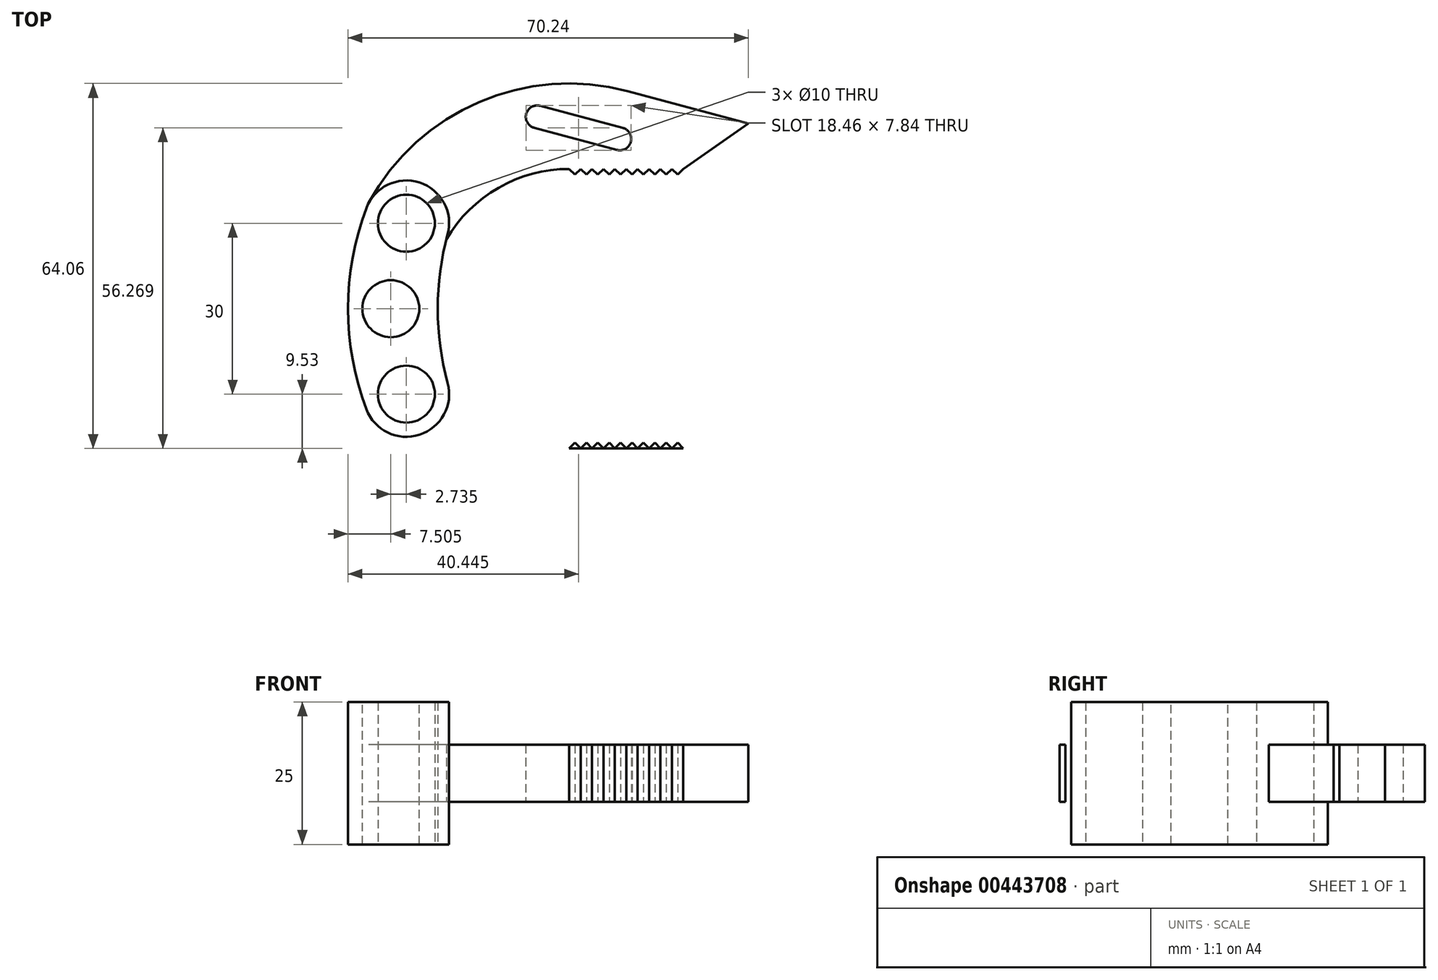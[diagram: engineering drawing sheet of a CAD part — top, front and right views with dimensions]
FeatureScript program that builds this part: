
annotation { "Feature Type Name" : "Feature", "Feature Type Description" : "" }
export const myFeature = defineFeature(function(context is Context, id is Id, definition is map)
    precondition{}
    {
        {
            var Q0;
            Q0=qCreatedBy(makeId("Top.planeOp"),FACE);
            var sketch = newSketch(context, id + "F0", { "sketchPlane" : qUnion([Q0])});
            skLineSegment(sketch, "E0", {"start": v(0, 15) * mm, "end": v(0, -15) * mm, "construction": true});
            skArc(sketch, "E1", {"start": v(7.24, 13.04) * mm, "mid": v(2.3, 22.14) * mm, "end": v(-7.02, 17.65) * mm});
            skArc(sketch, "E2", {"start": v(-7.02, -17.65) * mm, "mid": v(2.3, -22.14) * mm, "end": v(7.24, -13.04) * mm});
            skArc(sketch, "E3", {"start": v(-7.02, 17.65) * mm, "mid": v(-10.24, 0) * mm, "end": v(-7.02, -17.65) * mm});
            skArc(sketch, "E4", {"start": v(7.24, 13.04) * mm, "mid": v(5.5, 0) * mm, "end": v(7.24, -13.04) * mm});
            skCircle(sketch, "E5", {"center": v(0, 15) * mm, "radius": 5 * mm});
            skCircle(sketch, "E6", {"center": v(0, -15) * mm, "radius": 5 * mm});
            skSolve(sketch);
        }
        {
            var Q0;
            Q0=qCreatedBy(makeId("Top.planeOp"),FACE);
            var sketch = newSketch(context, id + "F1", { "sketchPlane" : qUnion([Q0])});
            skCircle(sketch, "E7.0", {"center": v(0, 15) * mm, "radius": 5 * mm});
            skArc(sketch, "E8", {"start": v(-6.6, 18.57) * mm, "mid": v(-3.57, 8.4) * mm, "end": v(6.6, 11.43) * mm});
            skArc(sketch, "E9", {"start": v(38.92, 38.17) * mm, "mid": v(12.76, 36.27) * mm, "end": v(-6.6, 18.57) * mm});
            skArc(sketch, "E10", {"start": v(28.58, 24.53) * mm, "mid": v(15.79, 21) * mm, "end": v(6.6, 11.43) * mm});
            skLineSegment(sketch, "E11", {"start": v(28.58, 24.53) * mm, "end": v(48.58, 24.53) * mm});
            skLineSegment(sketch, "E12", {"start": v(48.58, 24.53) * mm, "end": v(60, 32.53) * mm});
            skLineSegment(sketch, "E13", {"start": v(60, 32.53) * mm, "end": v(38.92, 38.17) * mm});
            skLineSegment(sketch, "E14", {"start": v(38.92, 38.17) * mm, "end": v(37.45, 29.8) * mm, "construction": true});
            skLineSegment(sketch, "E15", {"start": v(37.45, 29.8) * mm, "end": v(22.96, 33.68) * mm, "construction": true});
            skCircle(sketch, "E16", {"center": v(22.96, 33.68) * mm, "radius": 2 * mm});
            skCircle(sketch, "E17", {"center": v(37.45, 29.8) * mm, "radius": 2 * mm});
            skLineSegment(sketch, "E18", {"start": v(23.48, 35.6) * mm, "end": v(37.97, 31.73) * mm});
            skLineSegment(sketch, "E19", {"start": v(22.44, 31.75) * mm, "end": v(36.93, 27.87) * mm});
            skLineSegment(sketch, "E20", {"start": v(0, 0) * mm, "end": v(59.7, 0) * mm, "construction": true});
            skLineSegment(sketch, "E21", {"start": v(28.58, 24.53) * mm, "end": v(29.58, 23.53) * mm});
            skLineSegment(sketch, "E22", {"start": v(29.58, 23.53) * mm, "end": v(30.58, 24.53) * mm});
            skLineSegment(sketch, "E23.1.0.0", {"start": v(30.58, 24.53) * mm, "end": v(31.58, 23.53) * mm});
            skLineSegment(sketch, "E23.1.0.1", {"start": v(31.58, 23.53) * mm, "end": v(32.58, 24.53) * mm});
            skLineSegment(sketch, "E23.2.0.0", {"start": v(32.58, 24.53) * mm, "end": v(33.58, 23.53) * mm});
            skLineSegment(sketch, "E23.2.0.1", {"start": v(33.58, 23.53) * mm, "end": v(34.58, 24.53) * mm});
            skLineSegment(sketch, "E23.3.0.0", {"start": v(34.58, 24.53) * mm, "end": v(35.58, 23.53) * mm});
            skLineSegment(sketch, "E23.3.0.1", {"start": v(35.58, 23.53) * mm, "end": v(36.58, 24.53) * mm});
            skLineSegment(sketch, "E23.4.0.0", {"start": v(36.58, 24.53) * mm, "end": v(37.58, 23.53) * mm});
            skLineSegment(sketch, "E23.4.0.1", {"start": v(37.58, 23.53) * mm, "end": v(38.58, 24.53) * mm});
            skLineSegment(sketch, "E23.5.0.0", {"start": v(38.58, 24.53) * mm, "end": v(39.58, 23.53) * mm});
            skLineSegment(sketch, "E23.5.0.1", {"start": v(39.58, 23.53) * mm, "end": v(40.58, 24.53) * mm});
            skLineSegment(sketch, "E23.6.0.0", {"start": v(40.58, 24.53) * mm, "end": v(41.58, 23.53) * mm});
            skLineSegment(sketch, "E23.6.0.1", {"start": v(41.58, 23.53) * mm, "end": v(42.58, 24.53) * mm});
            skLineSegment(sketch, "E23.7.0.0", {"start": v(42.58, 24.53) * mm, "end": v(43.58, 23.53) * mm});
            skLineSegment(sketch, "E23.7.0.1", {"start": v(43.58, 23.53) * mm, "end": v(44.58, 24.53) * mm});
            skLineSegment(sketch, "E23.8.0.0", {"start": v(44.58, 24.53) * mm, "end": v(45.58, 23.53) * mm});
            skLineSegment(sketch, "E23.8.0.1", {"start": v(45.58, 23.53) * mm, "end": v(46.58, 24.53) * mm});
            skLineSegment(sketch, "E23.9.0.0", {"start": v(46.58, 24.53) * mm, "end": v(47.58, 23.53) * mm});
            skLineSegment(sketch, "E23.9.0.1", {"start": v(47.58, 23.53) * mm, "end": v(48.58, 24.53) * mm});
            skLineSegment(sketch, "E23.direction1", {"start": v(29.58, 23.53) * mm, "end": v(31.58, 23.53) * mm, "construction": true});
            skLineSegment(sketch, "E24.MirrorCS", {"start": v(29.58, -23.53) * mm, "end": v(30.58, -24.53) * mm});
            skLineSegment(sketch, "E25.MirrorCS", {"start": v(39.58, -23.53) * mm, "end": v(40.58, -24.53) * mm});
            skLineSegment(sketch, "E26.MirrorCS", {"start": v(30.58, -24.53) * mm, "end": v(31.58, -23.53) * mm});
            skLineSegment(sketch, "E27.MirrorCS", {"start": v(29.58, -23.53) * mm, "end": v(31.58, -23.53) * mm, "construction": true});
            skLineSegment(sketch, "E28.MirrorCS", {"start": v(32.58, -24.53) * mm, "end": v(33.58, -23.53) * mm});
            skLineSegment(sketch, "E29.MirrorCS", {"start": v(33.58, -23.53) * mm, "end": v(34.58, -24.53) * mm});
            skLineSegment(sketch, "E30.MirrorCS", {"start": v(41.58, -23.53) * mm, "end": v(42.58, -24.53) * mm});
            skLineSegment(sketch, "E31.MirrorCS", {"start": v(31.58, -23.53) * mm, "end": v(32.58, -24.53) * mm});
            skLineSegment(sketch, "E32.MirrorCS", {"start": v(40.58, -24.53) * mm, "end": v(41.58, -23.53) * mm});
            skLineSegment(sketch, "E33.MirrorCS", {"start": v(28.58, -24.53) * mm, "end": v(29.58, -23.53) * mm});
            skLineSegment(sketch, "E34.MirrorCS", {"start": v(45.58, -23.53) * mm, "end": v(46.58, -24.53) * mm});
            skLineSegment(sketch, "E35.MirrorCS", {"start": v(42.58, -24.53) * mm, "end": v(43.58, -23.53) * mm});
            skLineSegment(sketch, "E36.MirrorCS", {"start": v(36.58, -24.53) * mm, "end": v(37.58, -23.53) * mm});
            skLineSegment(sketch, "E37.MirrorCS", {"start": v(37.58, -23.53) * mm, "end": v(38.58, -24.53) * mm});
            skLineSegment(sketch, "E38.MirrorCS", {"start": v(38.58, -24.53) * mm, "end": v(39.58, -23.53) * mm});
            skLineSegment(sketch, "E39.MirrorCS", {"start": v(44.58, -24.53) * mm, "end": v(45.58, -23.53) * mm});
            skLineSegment(sketch, "E40.MirrorCS", {"start": v(35.58, -23.53) * mm, "end": v(36.58, -24.53) * mm});
            skLineSegment(sketch, "E41.MirrorCS", {"start": v(43.58, -23.53) * mm, "end": v(44.58, -24.53) * mm});
            skLineSegment(sketch, "E42.MirrorCS", {"start": v(34.58, -24.53) * mm, "end": v(35.58, -23.53) * mm});
            skLineSegment(sketch, "E43.MirrorCS", {"start": v(47.58, -23.53) * mm, "end": v(48.58, -24.53) * mm});
            skLineSegment(sketch, "E44.MirrorCS", {"start": v(28.58, -24.53) * mm, "end": v(48.58, -24.53) * mm});
            skLineSegment(sketch, "E45.MirrorCS", {"start": v(46.58, -24.53) * mm, "end": v(47.58, -23.53) * mm});
            skArc(sketch, "E46.MirrorCS", {"start": v(38.92, -38.17) * mm, "mid": v(12.76, -36.27) * mm, "end": v(-6.6, -18.57) * mm});
            skArc(sketch, "E47.MirrorCS", {"start": v(28.58, -24.53) * mm, "mid": v(15.79, -21) * mm, "end": v(6.6, -11.43) * mm});
            skCircle(sketch, "E48.MirrorC", {"center": v(0, -15) * mm, "radius": 5 * mm});
            skLineSegment(sketch, "E49.MirrorCS", {"start": v(60, -32.53) * mm, "end": v(38.92, -38.17) * mm});
            skLineSegment(sketch, "E50.MirrorCS", {"start": v(37.45, -29.8) * mm, "end": v(22.96, -33.68) * mm, "construction": true});
            skLineSegment(sketch, "E51.MirrorCS", {"start": v(38.92, -38.17) * mm, "end": v(37.45, -29.8) * mm, "construction": true});
            skCircle(sketch, "E52.MirrorC", {"center": v(22.96, -33.68) * mm, "radius": 2 * mm});
            skCircle(sketch, "E53.MirrorC", {"center": v(37.45, -29.8) * mm, "radius": 2 * mm});
            skLineSegment(sketch, "E54.MirrorCS", {"start": v(23.48, -35.6) * mm, "end": v(37.97, -31.73) * mm});
            skLineSegment(sketch, "E55.MirrorCS", {"start": v(48.58, -24.53) * mm, "end": v(60, -32.53) * mm});
            skLineSegment(sketch, "E56.MirrorCS", {"start": v(22.44, -31.75) * mm, "end": v(36.93, -27.87) * mm});
            skArc(sketch, "E57.MirrorCS", {"start": v(-6.6, -18.57) * mm, "mid": v(-3.57, -8.4) * mm, "end": v(6.6, -11.43) * mm});
            skSolve(sketch);
        }
        {
            var Q0;
            Q0=makeQuery(id+"F0.imprint","IMPRINT",FACE,{"disambiguationData":[TD([[makeQuery(id+"F0.imprint","IMPRINT",EDGE,{"derivedFrom":sQuery(id+"F0.wireOp",EDGE,"E1")}),1.0]])]});
            extrude(context, id + "F2", {"entities" : qUnion([Q0]), "endBound" : BoundingType.SYMMETRIC, "depth" : 25 * mm});
        }
        {
            var Q0;
            Q0=makeQuery(id+"F1.imprint","IMPRINT",FACE,{"disambiguationData":[TD([[makeQuery(id+"F1.imprint","IMPRINT",EDGE,{"derivedFrom":sQuery(id+"F1.wireOp",EDGE,"E7.0")}),-1.0]])]});
            var Q1;
            Q1=makeQuery(id+"F1.imprint","IMPRINT",FACE,{"disambiguationData":[TD([[makeQuery(id+"F1.imprint","IMPRINT",EDGE,{"derivedFrom":sQuery(id+"F1.wireOp",EDGE,"E46.MirrorCS")}),-1.0]])]});
            var Q2;
            {var subQ0=sQuery(id+"F1.wireOp",EDGE,"E21");Q2=makeQuery(id+"F1.imprint","IMPRINT",FACE,{"disambiguationData":[TD([[makeQuery(id+"F1.imprint","IMPRINT",EDGE,{"derivedFrom":subQ0}),1.0]])]});}
            var Q3;
            {var subQ0=sQuery(id+"F1.wireOp",EDGE,"E23.1.0.0");Q3=makeQuery(id+"F1.imprint","IMPRINT",FACE,{"disambiguationData":[TD([[makeQuery(id+"F1.imprint","IMPRINT",EDGE,{"derivedFrom":subQ0}),1.0]])]});}
            var Q4;
            {var subQ0=sQuery(id+"F1.wireOp",EDGE,"E23.2.0.0");Q4=makeQuery(id+"F1.imprint","IMPRINT",FACE,{"disambiguationData":[TD([[makeQuery(id+"F1.imprint","IMPRINT",EDGE,{"derivedFrom":subQ0}),1.0]])]});}
            var Q5;
            {var subQ0=sQuery(id+"F1.wireOp",EDGE,"E23.3.0.0");Q5=makeQuery(id+"F1.imprint","IMPRINT",FACE,{"disambiguationData":[TD([[makeQuery(id+"F1.imprint","IMPRINT",EDGE,{"derivedFrom":subQ0}),1.0]])]});}
            var Q6;
            {var subQ0=sQuery(id+"F1.wireOp",EDGE,"E23.4.0.0");Q6=makeQuery(id+"F1.imprint","IMPRINT",FACE,{"disambiguationData":[TD([[makeQuery(id+"F1.imprint","IMPRINT",EDGE,{"derivedFrom":subQ0}),1.0]])]});}
            var Q7;
            {var subQ0=sQuery(id+"F1.wireOp",EDGE,"E23.5.0.0");Q7=makeQuery(id+"F1.imprint","IMPRINT",FACE,{"disambiguationData":[TD([[makeQuery(id+"F1.imprint","IMPRINT",EDGE,{"derivedFrom":subQ0}),1.0]])]});}
            var Q8;
            {var subQ0=sQuery(id+"F1.wireOp",EDGE,"E23.6.0.0");Q8=makeQuery(id+"F1.imprint","IMPRINT",FACE,{"disambiguationData":[TD([[makeQuery(id+"F1.imprint","IMPRINT",EDGE,{"derivedFrom":subQ0}),1.0]])]});}
            var Q9;
            {var subQ0=sQuery(id+"F1.wireOp",EDGE,"E23.7.0.0");Q9=makeQuery(id+"F1.imprint","IMPRINT",FACE,{"disambiguationData":[TD([[makeQuery(id+"F1.imprint","IMPRINT",EDGE,{"derivedFrom":subQ0}),1.0]])]});}
            var Q10;
            {var subQ0=sQuery(id+"F1.wireOp",EDGE,"E23.8.0.0");Q10=makeQuery(id+"F1.imprint","IMPRINT",FACE,{"disambiguationData":[TD([[makeQuery(id+"F1.imprint","IMPRINT",EDGE,{"derivedFrom":subQ0}),1.0]])]});}
            var Q11;
            {var subQ2=sQuery(id+"F1.wireOp",EDGE,"E23.9.0.0");Q11=makeQuery(id+"F1.imprint","IMPRINT",FACE,{"disambiguationData":[TD([[makeQuery(id+"F1.imprint","IMPRINT",EDGE,{"derivedFrom":subQ2}),1.0]])]});}
            var Q12;
            {var subQ0=sQuery(id+"F1.wireOp",EDGE,"E24.MirrorCS");Q12=makeQuery(id+"F1.imprint","IMPRINT",FACE,{"disambiguationData":[TD([[makeQuery(id+"F1.imprint","IMPRINT",EDGE,{"derivedFrom":subQ0}),-1.0]])]});}
            var Q13;
            {var subQ0=sQuery(id+"F1.wireOp",EDGE,"E26.MirrorCS");Q13=makeQuery(id+"F1.imprint","IMPRINT",FACE,{"disambiguationData":[TD([[makeQuery(id+"F1.imprint","IMPRINT",EDGE,{"derivedFrom":subQ0}),-1.0]])]});}
            var Q14;
            {var subQ0=sQuery(id+"F1.wireOp",EDGE,"E28.MirrorCS");Q14=makeQuery(id+"F1.imprint","IMPRINT",FACE,{"disambiguationData":[TD([[makeQuery(id+"F1.imprint","IMPRINT",EDGE,{"derivedFrom":subQ0}),-1.0]])]});}
            var Q15;
            {var subQ0=sQuery(id+"F1.wireOp",EDGE,"E40.MirrorCS");Q15=makeQuery(id+"F1.imprint","IMPRINT",FACE,{"disambiguationData":[TD([[makeQuery(id+"F1.imprint","IMPRINT",EDGE,{"derivedFrom":subQ0}),-1.0]])]});}
            var Q16;
            {var subQ0=sQuery(id+"F1.wireOp",EDGE,"E36.MirrorCS");Q16=makeQuery(id+"F1.imprint","IMPRINT",FACE,{"disambiguationData":[TD([[makeQuery(id+"F1.imprint","IMPRINT",EDGE,{"derivedFrom":subQ0}),-1.0]])]});}
            var Q17;
            {var subQ0=sQuery(id+"F1.wireOp",EDGE,"E25.MirrorCS");Q17=makeQuery(id+"F1.imprint","IMPRINT",FACE,{"disambiguationData":[TD([[makeQuery(id+"F1.imprint","IMPRINT",EDGE,{"derivedFrom":subQ0}),-1.0]])]});}
            var Q18;
            {var subQ0=sQuery(id+"F1.wireOp",EDGE,"E30.MirrorCS");Q18=makeQuery(id+"F1.imprint","IMPRINT",FACE,{"disambiguationData":[TD([[makeQuery(id+"F1.imprint","IMPRINT",EDGE,{"derivedFrom":subQ0}),-1.0]])]});}
            var Q19;
            {var subQ0=sQuery(id+"F1.wireOp",EDGE,"E35.MirrorCS");Q19=makeQuery(id+"F1.imprint","IMPRINT",FACE,{"disambiguationData":[TD([[makeQuery(id+"F1.imprint","IMPRINT",EDGE,{"derivedFrom":subQ0}),-1.0]])]});}
            var Q20;
            {var subQ0=sQuery(id+"F1.wireOp",EDGE,"E34.MirrorCS");Q20=makeQuery(id+"F1.imprint","IMPRINT",FACE,{"disambiguationData":[TD([[makeQuery(id+"F1.imprint","IMPRINT",EDGE,{"derivedFrom":subQ0}),-1.0]])]});}
            var Q21;
            {var subQ0=sQuery(id+"F1.wireOp",EDGE,"E43.MirrorCS");Q21=makeQuery(id+"F1.imprint","IMPRINT",FACE,{"disambiguationData":[TD([[makeQuery(id+"F1.imprint","IMPRINT",EDGE,{"derivedFrom":subQ0}),-1.0]])]});}
            extrude(context, id + "F3", {"entities" : qUnion([Q0, Q1, Q2, Q3, Q4, Q5, Q6, Q7, Q8, Q9, Q10, Q11, Q12, Q13, Q14, Q15, Q16, Q17, Q18, Q19, Q20, Q21]), "operationType" : NewBodyOperationType.ADD, "endBound" : BoundingType.SYMMETRIC, "depth" : 10 * mm});
        }
        {
            var Q0;
            Q0=makeQuery(id+"F2.opExtrude","CAP_FACE",FACE,{"disambiguationData":[OSD([sQuery(id+"F0.wireOp",EDGE,"E1"),sQuery(id+"F0.wireOp",EDGE,"E2"),sQuery(id+"F0.wireOp",EDGE,"E3"),sQuery(id+"F0.wireOp",EDGE,"E4"),sQuery(id+"F0.wireOp",EDGE,"E5"),sQuery(id+"F0.wireOp",EDGE,"E6")])],"isStart":false});
            var sketch = newSketch(context, id + "F4", { "sketchPlane" : qUnion([Q0])});
            skArc(sketch, "E58", {"start": v(0, 15) * mm, "mid": v(-2.74, 0) * mm, "end": v(0, -15) * mm, "construction": true});
            skCircle(sketch, "E59", {"center": v(-2.74, 0) * mm, "radius": 5 * mm});
            skSolve(sketch);
        }
        {
            var Q0;
            Q0=makeQuery(id+"F4.imprint","IMPRINT",FACE,{"disambiguationData":[TD([[makeQuery(id+"F4.imprint","IMPRINT",EDGE,{"derivedFrom":sQuery(id+"F4.wireOp",EDGE,"E59")}),1.0]])]});
            var Q1;
            Q1=sQuery(id+"F4.wireOp",EDGE,"E59");
            extrude(context, id + "F5", {"entities" : qUnion([Q0]), "operationType" : NewBodyOperationType.REMOVE, "surfaceEntities" : qUnion([Q1]), "endBound" : BoundingType.THROUGH_ALL, "oppositeDirection" : true, "depth" : 25 * mm});
        }
    });
